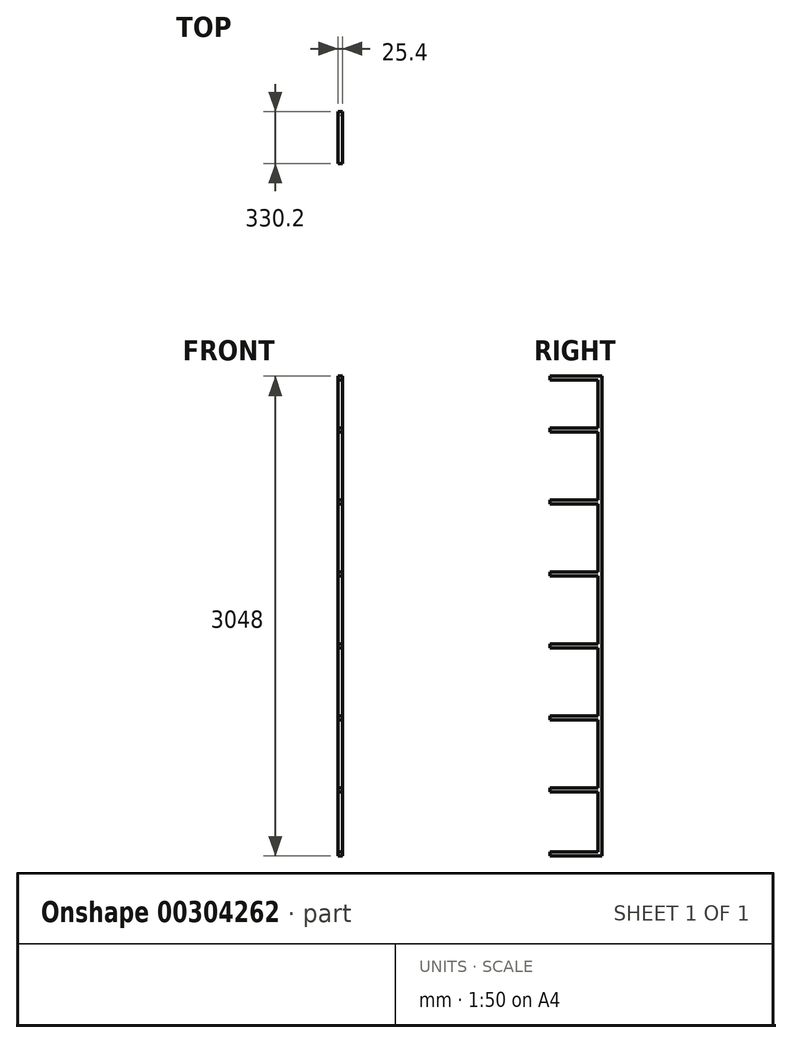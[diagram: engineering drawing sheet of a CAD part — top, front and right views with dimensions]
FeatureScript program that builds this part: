
annotation { "Feature Type Name" : "Feature", "Feature Type Description" : "" }
export const myFeature = defineFeature(function(context is Context, id is Id, definition is map)
    precondition{}
    {
        {
            var Q0;
            Q0=qCreatedBy(makeId("Right.planeOp"),FACE);
            var sketch = newSketch(context, id + "F0", { "sketchPlane" : qUnion([Q0])});
            skLineSegment(sketch, "E0.bottom", {"start": v(-330.2, 3048) * mm, "end": v(0, 3048) * mm});
            skLineSegment(sketch, "E0.top", {"start": v(-330.2, 0) * mm, "end": v(0, 0) * mm});
            skLineSegment(sketch, "E0.left", {"start": v(-330.2, 3048) * mm, "end": v(-330.2, 0) * mm, "construction": true});
            skLineSegment(sketch, "E0.right", {"start": v(0, 3048) * mm, "end": v(0, 0) * mm});
            skLineSegment(sketch, "E1.0", {"start": v(-330.2, 25.4) * mm, "end": v(-25.4, 25.4) * mm});
            skLineSegment(sketch, "E1.1", {"start": v(-25.4, 3022.6) * mm, "end": v(-25.4, 25.4) * mm});
            skLineSegment(sketch, "E1.2", {"start": v(-330.2, 3022.6) * mm, "end": v(-25.4, 3022.6) * mm});
            skLineSegment(sketch, "E2", {"start": v(-330.2, 406.4) * mm, "end": v(-330.2, 431.8) * mm});
            skLineSegment(sketch, "E3", {"start": v(-330.2, 3022.6) * mm, "end": v(-330.2, 3048) * mm});
            skLineSegment(sketch, "E4", {"start": v(-330.2, 431.8) * mm, "end": v(-25.4, 431.8) * mm});
            skLineSegment(sketch, "E5", {"start": v(-330.2, 406.4) * mm, "end": v(-25.4, 406.4) * mm});
            skLineSegment(sketch, "E6.0.1.0", {"start": v(-330.2, 863.6) * mm, "end": v(-330.2, 889) * mm});
            skLineSegment(sketch, "E6.0.1.1", {"start": v(-330.2, 863.6) * mm, "end": v(-25.4, 863.6) * mm});
            skLineSegment(sketch, "E6.0.1.2", {"start": v(-330.2, 889) * mm, "end": v(-25.4, 889) * mm});
            skLineSegment(sketch, "E6.0.2.0", {"start": v(-330.2, 1320.8) * mm, "end": v(-330.2, 1346.2) * mm});
            skLineSegment(sketch, "E6.0.2.1", {"start": v(-330.2, 1320.8) * mm, "end": v(-25.4, 1320.8) * mm});
            skLineSegment(sketch, "E6.0.2.2", {"start": v(-330.2, 1346.2) * mm, "end": v(-25.4, 1346.2) * mm});
            skLineSegment(sketch, "E6.0.3.0", {"start": v(-330.2, 1778) * mm, "end": v(-330.2, 1803.4) * mm});
            skLineSegment(sketch, "E6.0.3.1", {"start": v(-330.2, 1778) * mm, "end": v(-25.4, 1778) * mm});
            skLineSegment(sketch, "E6.0.3.2", {"start": v(-330.2, 1803.4) * mm, "end": v(-25.4, 1803.4) * mm});
            skLineSegment(sketch, "E6.0.4.0", {"start": v(-330.2, 2235.2) * mm, "end": v(-330.2, 2260.6) * mm});
            skLineSegment(sketch, "E6.0.4.1", {"start": v(-330.2, 2235.2) * mm, "end": v(-25.4, 2235.2) * mm});
            skLineSegment(sketch, "E6.0.4.2", {"start": v(-330.2, 2260.6) * mm, "end": v(-25.4, 2260.6) * mm});
            skLineSegment(sketch, "E6.0.5.0", {"start": v(-330.2, 2692.4) * mm, "end": v(-330.2, 2717.8) * mm});
            skLineSegment(sketch, "E6.0.5.1", {"start": v(-330.2, 2692.4) * mm, "end": v(-25.4, 2692.4) * mm});
            skLineSegment(sketch, "E6.0.5.2", {"start": v(-330.2, 2717.8) * mm, "end": v(-25.4, 2717.8) * mm});
            skLineSegment(sketch, "E6.direction1", {"start": v(-330.2, 406.4) * mm, "end": v(-355.6, 406.4) * mm, "construction": true});
            skLineSegment(sketch, "E6.direction2", {"start": v(-330.2, 406.4) * mm, "end": v(-330.2, 863.6) * mm, "construction": true});
            skLineSegment(sketch, "E7", {"start": v(-330.2, 0) * mm, "end": v(-330.2, 25.4) * mm});
            skSolve(sketch);
        }
        {
            var Q0;
            Q0 = qSketchRegion(id + "F0", true);
            extrude(context, id + "F1", {"entities" : qUnion([Q0]), "depth" : 25.4 * mm});
        }
    });
